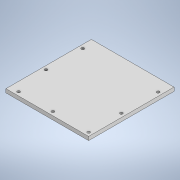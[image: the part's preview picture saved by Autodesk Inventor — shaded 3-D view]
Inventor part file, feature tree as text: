
AUTODESK INVENTOR PART (.ipt)
format: ipt  version: 2021 (Build 250183000, 183)  size: 117,248 bytes
history: native  units: mm
features: sketch x2, extrude x1, hole x1
ambient origin geometry x8: Origin, YZ Plane, XZ Plane, XY Plane, X Axis, Y Axis, Z Axis, Center Point
bodies: Solid1 (feature_tree)
feature tree (4):
  extrude  "Extrusion1"  Depth=116.2mm
  hole  "Hole1"  [1 undecoded]
  sketch  "Sketch1"  dims[d0=112.5mm d1=116.2mm]
  sketch  "Sketch3"  dims[d2=5.0mm d3=0.0mm d21=5.0mm d22=5.0mm d23=5.0mm d26=3.8mm d27=6.0mm d28=4.0mm d29=2.0mm d30=90.0deg d31=8.0mm d32=20.594885mm d34=12.3mm d35=58.9mm d36=107.5mm d37=49.5mm d38=99.5mm]
note: 1 required parameter value undecoded (feature->parameter linkage not recoverable at this tier; creation-order binding heuristic only, values carry confidence <= 0.55)
